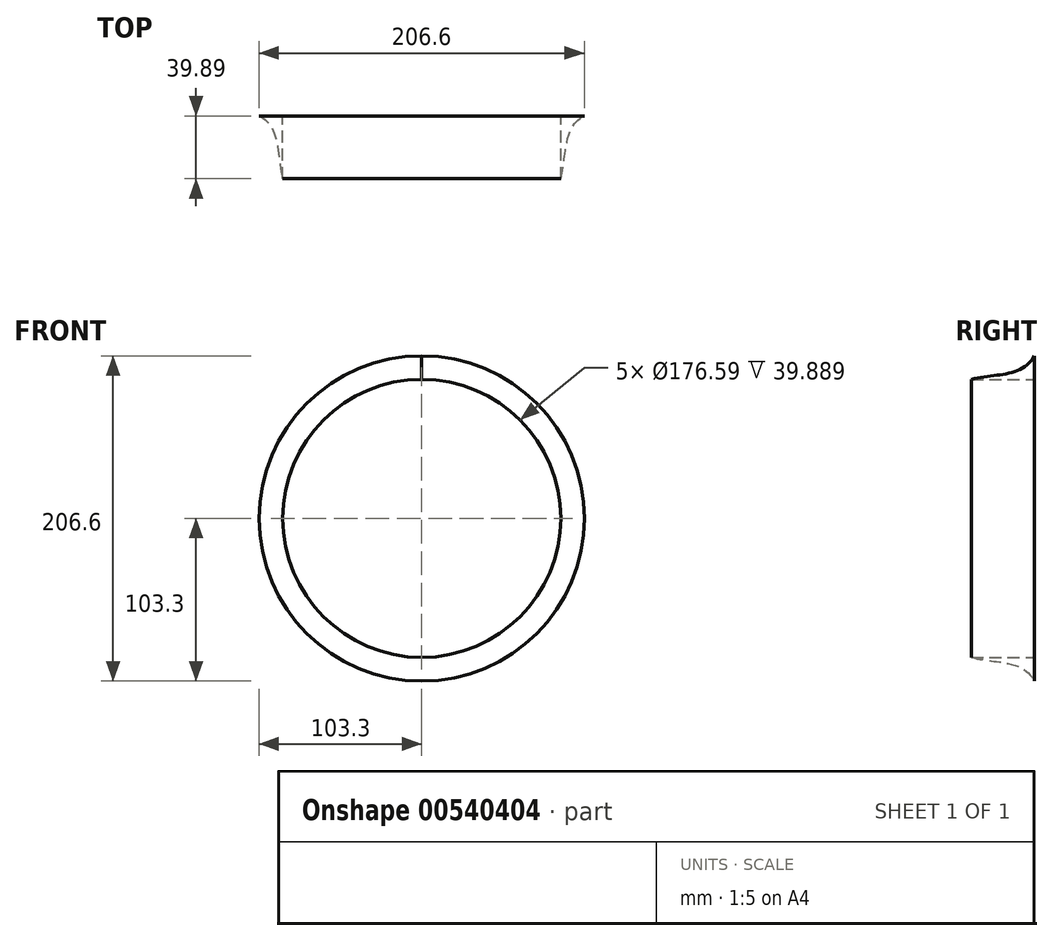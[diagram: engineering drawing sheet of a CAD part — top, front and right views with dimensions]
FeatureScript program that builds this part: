
annotation { "Feature Type Name" : "Feature", "Feature Type Description" : "" }
export const myFeature = defineFeature(function(context is Context, id is Id, definition is map)
    precondition{}
    {
        {
            var Q0;
            Q0=qCreatedBy(makeId("Right.planeOp"),FACE);
            var sketch = newSketch(context, id + "F0", { "sketchPlane" : qUnion([Q0])});
            skLineSegment(sketch, "E0", {"start": v(0, 0) * mm, "end": v(0, -88.3) * mm});
            skLineSegment(sketch, "E1", {"start": v(0, -88.3) * mm, "end": v(-39.89, -88.3) * mm});
            skLineSegment(sketch, "E2", {"start": v(0, -103.3) * mm, "end": v(0, -88.3) * mm});
            skFitSpline(sketch, "E3", {"points": [v(-39.89, -88.3) * mm, v(0, -103.3) * mm, v(-39.89, -286.79) * mm, v(-67.19, -327.97) * mm], "startDerivative": vector(188.34, -49.83) * mm, "endDerivative": vector(-117.53, -32.7) * mm});
            skLineSegment(sketch, "E4", {"start": v(0, 0) * mm, "end": v(-49.16, 0) * mm});
            skSolve(sketch);
        }
        {
            var Q0;
            Q0 = qSketchRegion(id + "F0", true);
            var Q1;
            Q1=sQuery(id+"F0.wireOp",EDGE,"E4");
            revolve(context, id + "F1", {"entities" : qUnion([Q0]), "axis" : qUnion([Q1]), "revolveType" : RevolveType.FULL});
        }
    });
